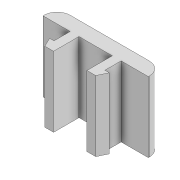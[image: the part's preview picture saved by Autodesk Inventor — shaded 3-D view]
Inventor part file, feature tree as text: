
AUTODESK INVENTOR PART (.ipt)
format: ipt  version: 2021 (Build 250183000, 183)  size: 142,848 bytes
history: native  units: mm
features: reference x10, extrude x4, sketch x4, other x2, direct_edit x1, fillet x1, move_body x1
ambient origin geometry x8: Origin, YZ Plane, XZ Plane, XY Plane, X Axis, Y Axis, Z Axis, Center Point
bodies: Volumenkörper1 (feature_tree)
feature tree (23):
  extrude  "Extrusion1"  Depth=20.0mm
  extrude  "Extrusion2"  TaperAngle=0.0deg  [1 undecoded]
  extrude  "Extrusion3"  Depth=12.0mm
  extrude  "Extrusion6"  TaperAngle=0.0deg  [1 undecoded]
  direct_edit  "Direktbearbeitung2"
  fillet  "Rundung5"  [1 undecoded]
  sketch  "Skizze1"  dims[d0=20.0mm d1=20.0mm]
  sketch  "Skizze2"  dims[d2=34.5mm d3=0.0mm d4=0.0mm d5=0.0mm]
  sketch  "Skizze3"  dims[d6=10.0mm d7=0.0mm d26=12.0mm]
  reference  "Referenz4"
  reference  "Referenz5"
  reference  "Referenz6"
  reference  "Referenz7"
  reference  "Referenz8"
  reference  "Referenz9"
  reference  "Referenz10"
  reference  "Referenz11"
  reference  "Referenz12"
  reference  "Referenz13"
  sketch  "Skizze6"  dims[d27=3.2mm d28=0.0mm d29=0.0mm d30=0.0mm d31=0.0mm d32=-26.5mm d33=1.5mm]
  other  "Baugruppe2"
  other  "Light_Bar_Clip_-_Misumi (1):1"
  move_body  "Verschieben2"
note: 3 required parameter values undecoded (feature->parameter linkage not recoverable at this tier; creation-order binding heuristic only, values carry confidence <= 0.55)
